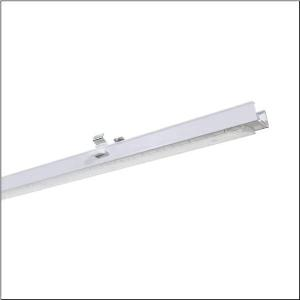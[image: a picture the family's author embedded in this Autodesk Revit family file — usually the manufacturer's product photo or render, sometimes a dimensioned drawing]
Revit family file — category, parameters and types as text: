
# Revit family: trunking_flex_31_51re11mb4cb
name_source: partatom
category: Lighting Fixtures
units: mm (PartAtom-declared; Revit-internal decimal feet)

## family parameters
Cut with Voids When Loaded = No
Host = Face
Light Source = No
Part Type = Normal
Room Calculation Point = No
Round Connector Dimension = Use Diameter
Shared = No

## types (1)
- --- (1 x LED, 11500 lm, 66 W, 4000K)
    Apparent Load = 66 VA
    CIE Flux Codes = 83 93 98 100 100
    Color Rendering = 80
    Color Temperature = 4000K
    Default Elevation = 1800 mm
    Description = Trunking Flex 31, luminaire insert, of extruded aluminium section, coated, traffic white (RAL 9016), length: 1.472mm, width: 91mm, height: 53mm, LED rated luminous flux: 11.500lm, light colour: 840, control gear: ON/OFF Multilumen, with system connector: socket, mains connection: 220..240V, AC, 50/60Hz, rated input power: 66W, luminous flux adjustable on luminaire in eight steps (3450/4380/5800/6700/8350/9200/10500/11500lm ), connected load according to luminous flux setting (19/24/32/37/47/52/60/66W), primary light control with lens, of plastic, primary optical cover: cover, of PMMA, light emission: direct distribution, protection rating (complete): IP20, insulation class (complete): insulation class I (protective earthing), certification: CE, UKCA, impact resistance: IK02, permissible ambient temperature for indoor applications: -20..+40°C, packaging unit: 1 piece
    Height = 58 mm
    Lamp = 1 x LED
    Lamp Light Flux = 11500 lm
    Lamp Power = 66 W
    Lamp count = 1
    Length = 1472 mm
    Luminous efficacy = 174 lm/W
    Manufacturer = Siteco
    ModVariant = No
    Model = 51RE11MB4CB
    Mounting Place = Ceiling
    Mounting Type = Pendant
    Number of Poles = 1
    OnlyDefault = Yes
    Power Factor = 1
    Product Name = Trunking Flex 31
    Product group = luminaire insert
    ProductGroupID = 901
    Protection Class = Protection class I
    Protection Degree = IP 20
    RLX_Detail_Level = 1
    RLX_Emergency_Light_Flux = 0 lm
    RLX_Emergency_Type = 0
    RLX_Emergency_Type_DB = No
    RlxData = <blob elided: 20949 chars, md5=5385393b>
    Socket = socket
    Standby Power = 0 W
    System Light Flux = 11500 lm
    System Power = 66 W
    Type Comments = factory setting: luminous flux: 100 % | (ON | ON | ON)
    Type Image = l_1266702.jpg
    URL = http://relux.com
    VarID = @adj_001391
    Voltage = 0 V
    Weight = 0.00 kg
    Width = 65 mm

## geometry (parser evidence)
native form markers: Blend x4, Sweep x11
no freeform markers — native parametric forms only
